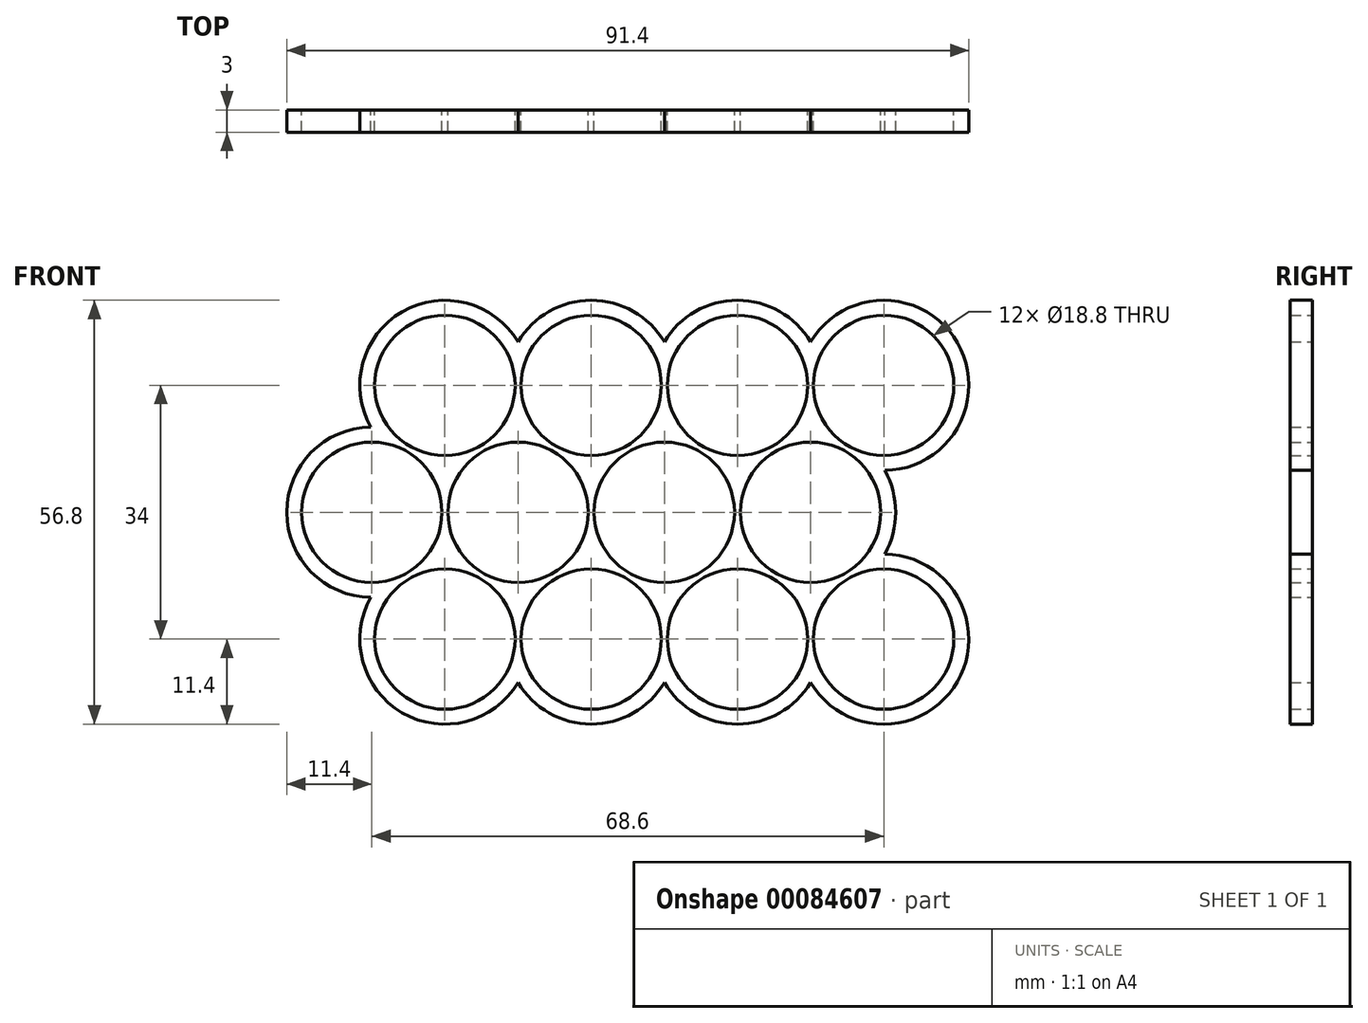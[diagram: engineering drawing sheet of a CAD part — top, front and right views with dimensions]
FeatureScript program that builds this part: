
annotation { "Feature Type Name" : "Feature", "Feature Type Description" : "" }
export const myFeature = defineFeature(function(context is Context, id is Id, definition is map)
    precondition{}
    {
        {
            var Q0;
            Q0=qCreatedBy(makeId("Front.planeOp"),FACE);
            var sketch = newSketch(context, id + "F0", { "sketchPlane" : qUnion([Q0]) });
            skCircle(sketch, "E0.1.0.0", {"center": v(19.6, 0) * mm, "radius": 9.4 * mm});
            skCircle(sketch, "E0.2.0.0", {"center": v(39.2, 0) * mm, "radius": 9.4 * mm});
            skArc(sketch, "E0.3.0.0", {"start": v(58.8, 9.4) * mm, "mid": v(54.1, -8.14) * mm, "end": v(66.94, 4.7) * mm});
            skLineSegment(sketch, "E0.direction1", {"start": v(0, 0) * mm, "end": v(19.6, 0) * mm, "construction": true});
            skLineSegment(sketch, "E1", {"start": v(0, -17) * mm, "end": v(73.2, -17) * mm, "construction": true});
            skLineSegment(sketch, "E2", {"start": v(9.8, 0) * mm, "end": v(9.8, -17) * mm, "construction": true});
            skCircle(sketch, "E3", {"center": v(9.8, -17) * mm, "radius": 9.4 * mm});
            skCircle(sketch, "E4.1.0.0", {"center": v(29.4, -17) * mm, "radius": 9.4 * mm});
            skCircle(sketch, "E4.2.0.0", {"center": v(49, -17) * mm, "radius": 9.4 * mm});
            skCircle(sketch, "E4.3.0.0", {"center": v(68.6, -17) * mm, "radius": 9.4 * mm});
            skLineSegment(sketch, "E4.direction1", {"start": v(9.8, -17) * mm, "end": v(29.4, -17) * mm, "construction": true});
            skLineSegment(sketch, "E5", {"start": v(9.8, -17) * mm, "end": v(9.8, -26.4) * mm, "construction": true});
            skLineSegment(sketch, "E6", {"start": v(68.6, -17) * mm, "end": v(68.6, -26.4) * mm, "construction": true});
            skArc(sketch, "E7", {"start": v(58.8, 9.4) * mm, "mid": v(63.5, 8.14) * mm, "end": v(66.94, 4.7) * mm});
            skArc(sketch, "E8", {"start": v(76.74, -12.3) * mm, "mid": v(76.74, -21.7) * mm, "end": v(68.6, -26.4) * mm});
            skArc(sketch, "E9", {"start": v(9.8, -26.4) * mm, "mid": v(5.1, -25.14) * mm, "end": v(1.66, -21.7) * mm});
            skArc(sketch, "E10.trimOffspring", {"start": v(9.8, -5.82) * mm, "mid": v(9.87, -5.71) * mm, "end": v(9.93, -5.6) * mm});
            skArc(sketch, "E11.trimOffspring", {"start": v(9.93, -5.6) * mm, "mid": v(9.86, -5.6) * mm, "end": v(9.8, -5.6) * mm});
            skCircle(sketch, "E12.0.4.0", {"center": v(78.4, 0) * mm, "radius": 9.4 * mm});
            skLineSegment(sketch, "E13", {"start": v(0, 0) * mm, "end": v(9.8, -17) * mm, "construction": true});
            skCircle(sketch, "E14.1.0.0", {"center": v(19.6, -34) * mm, "radius": 9.4 * mm});
            skLineSegment(sketch, "E14.direction1", {"start": v(9.8, -17) * mm, "end": v(19.6, -34) * mm, "construction": true});
            skCircle(sketch, "E15.1.0.0", {"center": v(39.2, -34) * mm, "radius": 9.4 * mm});
            skCircle(sketch, "E15.2.0.0", {"center": v(58.8, -34) * mm, "radius": 9.4 * mm});
            skCircle(sketch, "E15.3.0.0", {"center": v(78.4, -34) * mm, "radius": 9.4 * mm});
            skLineSegment(sketch, "E15.direction1", {"start": v(19.6, -34) * mm, "end": v(39.2, -34) * mm, "construction": true});
            skPoint(sketch, "E16.start.orphan", {"position": v(0, 9.4) * mm});
            skArc(sketch, "E17.0", {"start": v(29.4, 5.82) * mm, "mid": v(13.78, 9.8) * mm, "end": v(9.8, -5.82) * mm});
            skArc(sketch, "E18.0", {"start": v(58.8, 11.4) * mm, "mid": v(64.5, 9.87) * mm, "end": v(68.68, 5.7) * mm});
            skArc(sketch, "E18.1", {"start": v(58.8, 11.4) * mm, "mid": v(53.16, 9.9) * mm, "end": v(49, 5.82) * mm});
            skArc(sketch, "E19.0", {"start": v(9.67, -28.4) * mm, "mid": v(13.89, -43.87) * mm, "end": v(29.4, -39.82) * mm});
            skArc(sketch, "E20.trimOffspring", {"start": v(49, 5.82) * mm, "mid": v(39.2, 11.4) * mm, "end": v(29.4, 5.82) * mm});
            skArc(sketch, "E21.trimOffspring", {"start": v(9.93, -5.6) * mm, "mid": v(-1.6, -16.87) * mm, "end": v(9.67, -28.4) * mm});
            skArc(sketch, "E22.trimOffspring", {"start": v(78.53, -11.4) * mm, "mid": v(88.28, 5.7) * mm, "end": v(68.6, 5.82) * mm});
            skArc(sketch, "E23.trimOffspring", {"start": v(78.53, -22.6) * mm, "mid": v(80, -17) * mm, "end": v(78.53, -11.4) * mm});
            skArc(sketch, "E24.trimOffspring", {"start": v(68.6, -39.82) * mm, "mid": v(88.28, -39.7) * mm, "end": v(78.53, -22.6) * mm});
            skArc(sketch, "E25.trimOffspring", {"start": v(49, -39.82) * mm, "mid": v(58.8, -45.4) * mm, "end": v(68.6, -39.82) * mm});
            skArc(sketch, "E26.trimOffspring", {"start": v(29.4, -39.82) * mm, "mid": v(39.2, -45.4) * mm, "end": v(49, -39.82) * mm});
            skLineSegment(sketch, "E27", {"start": v(-1.6, -17.13) * mm, "end": v(-2, 18.34) * mm, "construction": true});
            skPoint(sketch, "E27.startSnap0", {"position": v(-1.6, -16.87) * mm});
            skLineSegment(sketch, "E28", {"start": v(58.8, 11.4) * mm, "end": v(-1.92, 11.4) * mm, "construction": true});
            skLineSegment(sketch, "E29.bottom", {"start": v(-1.92, 11.4) * mm, "end": v(89.9, 11.4) * mm, "construction": true});
            skLineSegment(sketch, "E29.top", {"start": v(-1.92, -45.46) * mm, "end": v(89.9, -45.46) * mm, "construction": true});
            skLineSegment(sketch, "E29.left", {"start": v(-1.92, 11.4) * mm, "end": v(-1.92, -45.46) * mm, "construction": true});
            skLineSegment(sketch, "E29.right", {"start": v(89.9, 11.4) * mm, "end": v(89.9, -45.46) * mm, "construction": true});
            skSolve(sketch);
        }
        {
            var Q0;
            Q0=qSketchRegion(id+"F0",true);
            var Q1;
            {var subQ3=sQuery(id+"F0.wireOp",EDGE,"E0.1.0.0");Q1=makeQuery(id+"F0.imprint","IMPRINT",FACE,{"disambiguationData":[TD([[makeQuery(id+"F0.imprint","IMPRINT",EDGE,{"derivedFrom":subQ3}),-1.0]])]});}
            extrude(context, id + "F1", {"entities" : qUnion([Q0, Q1]), "depth" : 3 * mm});
        }
    });
